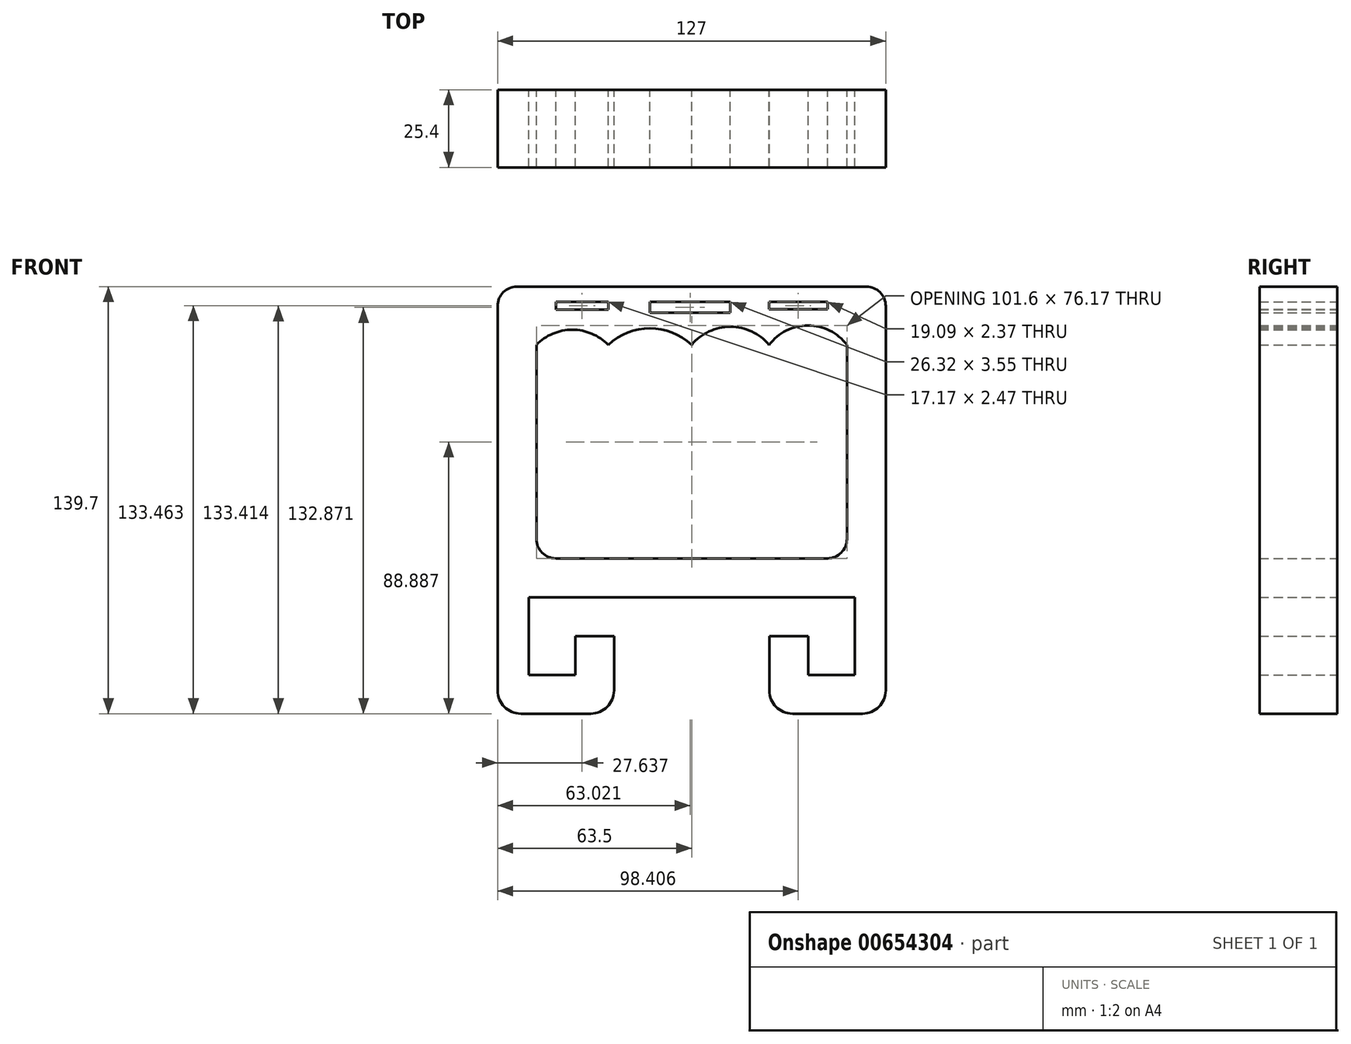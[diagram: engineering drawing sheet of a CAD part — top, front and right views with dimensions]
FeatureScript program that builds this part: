
annotation { "Feature Type Name" : "Feature", "Feature Type Description" : "" }
export const myFeature = defineFeature(function(context is Context, id is Id, definition is map)
    precondition{}
    {
        {
            var Q0;
            Q0=qCreatedBy(makeId("Front.planeOp"),FACE);
            var sketch = newSketch(context, id + "F0", { "sketchPlane" : qUnion([Q0])});
            skPoint(sketch, "E0.middle", {"position": v(0, 0) * mm});
            skLineSegment(sketch, "E1.bottom", {"start": v(57.15, 50.8) * mm, "end": v(-57.15, 50.8) * mm});
            skLineSegment(sketch, "E1.top", {"start": v(63.5, -50.8) * mm, "end": v(-63.5, -50.8) * mm});
            skLineSegment(sketch, "E1.left", {"start": v(63.5, 44.45) * mm, "end": v(63.5, -50.8) * mm});
            skLineSegment(sketch, "E1.right", {"start": v(-63.5, 44.45) * mm, "end": v(-63.5, -50.8) * mm});
            skLineSegment(sketch, "E2.top", {"start": v(-58.33, -39.2) * mm, "end": v(63.5, -39.2) * mm});
            skLineSegment(sketch, "E2.left", {"start": v(-58.33, 62.11) * mm, "end": v(-58.33, -39.2) * mm});
            skLineSegment(sketch, "E3", {"start": v(-63.5, -50.8) * mm, "end": v(-58.33, -39.2) * mm});
            skLineSegment(sketch, "E4", {"start": v(55.88, -88.9) * mm, "end": v(33.02, -88.9) * mm});
            skLineSegment(sketch, "E5", {"start": v(25.4, -81.28) * mm, "end": v(25.4, -63.5) * mm});
            skLineSegment(sketch, "E6", {"start": v(25.4, -63.5) * mm, "end": v(38.1, -63.5) * mm});
            skLineSegment(sketch, "E7", {"start": v(38.1, -63.5) * mm, "end": v(38.1, -76.2) * mm});
            skLineSegment(sketch, "E8", {"start": v(38.1, -76.2) * mm, "end": v(53.34, -76.2) * mm});
            skLineSegment(sketch, "E9", {"start": v(53.34, -76.2) * mm, "end": v(53.34, -50.8) * mm});
            skLineSegment(sketch, "E10.MirrorCS", {"start": v(-25.4, -81.28) * mm, "end": v(-25.4, -63.5) * mm});
            skLineSegment(sketch, "E11.MirrorCS", {"start": v(-25.4, -63.5) * mm, "end": v(-38.1, -63.5) * mm});
            skLineSegment(sketch, "E12.MirrorCS", {"start": v(-38.1, -63.5) * mm, "end": v(-38.1, -76.2) * mm});
            skLineSegment(sketch, "E13.MirrorCS", {"start": v(-38.1, -76.2) * mm, "end": v(-53.34, -76.2) * mm});
            skLineSegment(sketch, "E14.MirrorCS", {"start": v(-53.34, -76.2) * mm, "end": v(-53.34, -50.8) * mm});
            skLineSegment(sketch, "E15.MirrorCS", {"start": v(-63.5, -50.8) * mm, "end": v(-63.5, -81.28) * mm});
            skLineSegment(sketch, "E16.MirrorCS", {"start": v(-55.88, -88.9) * mm, "end": v(-33.02, -88.9) * mm});
            skPoint(sketch, "E17.visualSharp", {"position": v(-63.5, -88.9) * mm});
            skArc(sketch, "E17.filletArc", {"start": v(-63.5, -81.28) * mm, "mid": v(-61.27, -86.67) * mm, "end": v(-55.88, -88.9) * mm});
            skPoint(sketch, "E18.visualSharp", {"position": v(-25.4, -88.9) * mm});
            skArc(sketch, "E18.filletArc", {"start": v(-33.02, -88.9) * mm, "mid": v(-27.63, -86.67) * mm, "end": v(-25.4, -81.28) * mm});
            skPoint(sketch, "E19.visualSharp", {"position": v(25.4, -88.9) * mm});
            skArc(sketch, "E19.filletArc", {"start": v(25.4, -81.28) * mm, "mid": v(27.63, -86.67) * mm, "end": v(33.02, -88.9) * mm});
            skPoint(sketch, "E20.visualSharp", {"position": v(63.5, -88.9) * mm});
            skArc(sketch, "E20.filletArc", {"start": v(55.88, -88.9) * mm, "mid": v(61.27, -86.67) * mm, "end": v(63.5, -81.28) * mm});
            skLineSegment(sketch, "E21", {"start": v(63.5, -50.8) * mm, "end": v(69.65, -50.8) * mm});
            skLineSegment(sketch, "E22", {"start": v(63.5, -81.28) * mm, "end": v(63.5, -50.8) * mm});
            skLineSegment(sketch, "E23.bottom", {"start": v(44.45, 38.1) * mm, "end": v(-44.45, 38.1) * mm});
            skLineSegment(sketch, "E23.top", {"start": v(44.45, -38.1) * mm, "end": v(-44.45, -38.1) * mm});
            skLineSegment(sketch, "E23.left", {"start": v(50.8, 31.75) * mm, "end": v(50.8, -31.75) * mm});
            skLineSegment(sketch, "E23.right", {"start": v(-50.8, 31.75) * mm, "end": v(-50.8, -31.75) * mm});
            skPoint(sketch, "E24.visualSharp", {"position": v(-50.8, 38.1) * mm});
            skArc(sketch, "E24.filletArc", {"start": v(-44.45, 38.1) * mm, "mid": v(-48.94, 36.24) * mm, "end": v(-50.8, 31.75) * mm});
            skPoint(sketch, "E25.visualSharp", {"position": v(-63.5, 50.8) * mm});
            skArc(sketch, "E25.filletArc", {"start": v(-57.15, 50.8) * mm, "mid": v(-61.64, 48.94) * mm, "end": v(-63.5, 44.45) * mm});
            skPoint(sketch, "E26.visualSharp", {"position": v(50.8, 38.1) * mm});
            skArc(sketch, "E26.filletArc", {"start": v(50.8, 31.75) * mm, "mid": v(48.94, 36.24) * mm, "end": v(44.45, 38.1) * mm});
            skPoint(sketch, "E27.visualSharp", {"position": v(63.5, 50.8) * mm});
            skArc(sketch, "E27.filletArc", {"start": v(63.5, 44.45) * mm, "mid": v(61.64, 48.94) * mm, "end": v(57.15, 50.8) * mm});
            skArc(sketch, "E28.MirrorCS", {"start": v(-44.45, -38.1) * mm, "mid": v(-48.94, -36.24) * mm, "end": v(-50.8, -31.75) * mm});
            skArc(sketch, "E29.MirrorCS", {"start": v(50.8, -31.75) * mm, "mid": v(48.94, -36.24) * mm, "end": v(44.45, -38.1) * mm});
            skPoint(sketch, "E30.orphan", {"position": v(-50.8, -38.1) * mm});
            skPoint(sketch, "E31.orphan", {"position": v(50.8, -38.1) * mm});
            skArc(sketch, "E32", {"start": v(50.8, 31.75) * mm, "mid": v(38.08, 38.07) * mm, "end": v(25.36, 31.75) * mm});
            skArc(sketch, "E33", {"start": v(25.36, 31.75) * mm, "mid": v(12.68, 37.66) * mm, "end": v(0, 31.75) * mm});
            skArc(sketch, "E34", {"start": v(-27.28, 31.75) * mm, "mid": v(-39.04, 36.68) * mm, "end": v(-50.8, 31.75) * mm});
            skArc(sketch, "E35", {"start": v(0, 31.75) * mm, "mid": v(-13.64, 37.13) * mm, "end": v(-27.28, 31.75) * mm});
            skLineSegment(sketch, "E36.bottom", {"start": v(44.45, 45.75) * mm, "end": v(25.36, 45.75) * mm});
            skLineSegment(sketch, "E36.top", {"start": v(44.45, 43.38) * mm, "end": v(25.36, 43.38) * mm});
            skLineSegment(sketch, "E36.left", {"start": v(44.45, 45.75) * mm, "end": v(44.45, 43.38) * mm});
            skLineSegment(sketch, "E36.right", {"start": v(25.36, 45.75) * mm, "end": v(25.36, 43.38) * mm});
            skLineSegment(sketch, "E37.bottom", {"start": v(-44.45, 45.75) * mm, "end": v(-27.28, 45.75) * mm});
            skLineSegment(sketch, "E37.top", {"start": v(-44.45, 43.28) * mm, "end": v(-27.28, 43.28) * mm});
            skLineSegment(sketch, "E37.left", {"start": v(-44.45, 45.75) * mm, "end": v(-44.45, 43.28) * mm});
            skLineSegment(sketch, "E37.right", {"start": v(-27.28, 45.75) * mm, "end": v(-27.28, 43.28) * mm});
            skPoint(sketch, "E38.firstSnap0", {"position": v(12.68, 37.66) * mm});
            skPoint(sketch, "E38.oppositeSnap0", {"position": v(-13.64, 37.13) * mm});
            skLineSegment(sketch, "E38.bottom", {"start": v(12.68, 45.75) * mm, "end": v(-13.64, 45.75) * mm});
            skLineSegment(sketch, "E38.top", {"start": v(12.68, 42.2) * mm, "end": v(-13.64, 42.2) * mm});
            skLineSegment(sketch, "E38.left", {"start": v(12.68, 45.75) * mm, "end": v(12.68, 42.2) * mm});
            skLineSegment(sketch, "E38.right", {"start": v(-13.64, 45.75) * mm, "end": v(-13.64, 42.2) * mm});
            skSolve(sketch);
        }
        {
            var Q0;
            Q0 = qSketchRegion(id + "F0", true);
            var Q1;
            Q1=makeQuery(id+"F0.imprint","IMPRINT",FACE,{"disambiguationData":[TD([[makeQuery(id+"F0.imprint","IMPRINT",EDGE,{"derivedFrom":sQuery(id+"F0.wireOp",EDGE,"E23.bottom")}),1.0]])]});
            extrude(context, id + "F1", {"entities" : qUnion([Q0, Q1]), "depth" : 25.4 * mm, "offsetDistance" : 25.4 * mm});
        }
    });
